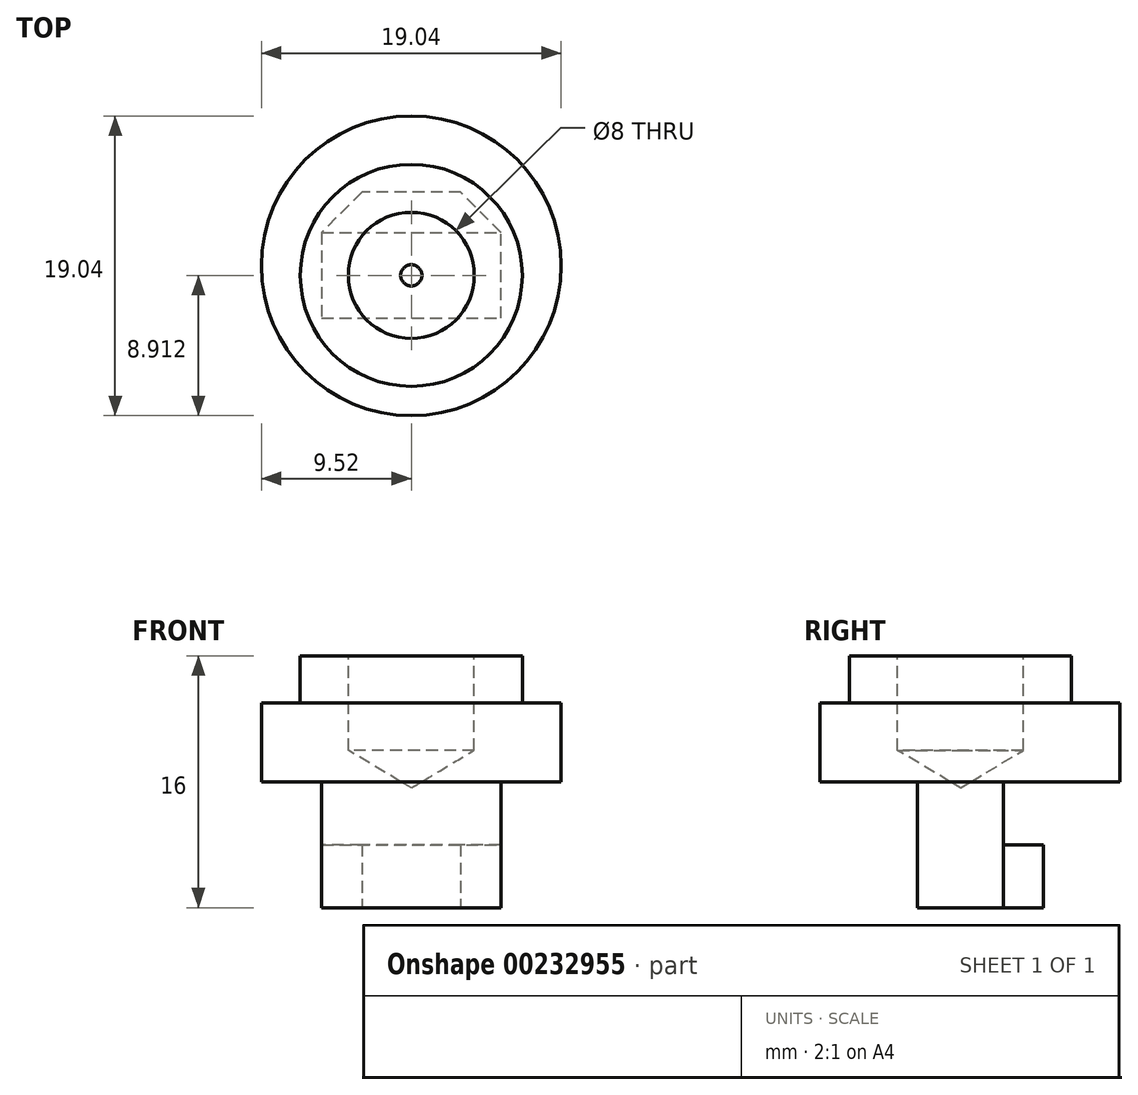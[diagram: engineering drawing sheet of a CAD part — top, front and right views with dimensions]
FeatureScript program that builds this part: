
annotation { "Feature Type Name" : "Feature", "Feature Type Description" : "" }
export const myFeature = defineFeature(function(context is Context, id is Id, definition is map)
    precondition{}
    {
        {
            var Q0;
            Q0=qCreatedBy(makeId("Top.planeOp"),FACE);
            var sketch = newSketch(context, id + "F4", { "sketchPlane" : qUnion([Q0])});
            skLineSegment(sketch, "E0", {"start": v(-5.7, -5.44) * mm, "end": v(5.7, -5.44) * mm});
            skLineSegment(sketch, "E1", {"start": v(5.7, -5.44) * mm, "end": v(5.7, 0) * mm});
            skLineSegment(sketch, "E2", {"start": v(5.7, 0) * mm, "end": v(3.14, 2.56) * mm});
            skLineSegment(sketch, "E3", {"start": v(3.14, 2.56) * mm, "end": v(-3.14, 2.56) * mm});
            skLineSegment(sketch, "E4", {"start": v(-3.14, 2.56) * mm, "end": v(-5.7, 0) * mm});
            skLineSegment(sketch, "E5", {"start": v(-5.7, 0) * mm, "end": v(-5.7, -5.44) * mm});
            skLineSegment(sketch, "E6", {"start": v(-3.14, 2.56) * mm, "end": v(-3.14, -5.44) * mm, "construction": true});
            skSolve(sketch);
        }
        {
            var Q0;
            Q0=makeQuery(id+"F4.imprint","IMPRINT",FACE,{"disambiguationData":[TD([[makeQuery(id+"F4.imprint","IMPRINT",EDGE,{"derivedFrom":sQuery(id+"F4.wireOp",EDGE,"E0")}),1.0]])]});
            extrude(context, id + "F0", {"entities" : qUnion([Q0]), "depth" : 4 * mm});
        }
        {
            var Q0;
            Q0=makeQuery(id+"F0.opExtrude","CAP_FACE",FACE,{"disambiguationData":[OSD([sQuery(id+"F4.wireOp",EDGE,"E0"),sQuery(id+"F4.wireOp",EDGE,"E1"),sQuery(id+"F4.wireOp",EDGE,"E2"),sQuery(id+"F4.wireOp",EDGE,"E3"),sQuery(id+"F4.wireOp",EDGE,"E4"),sQuery(id+"F4.wireOp",EDGE,"E5")])],"isStart":false});
            var sketch = newSketch(context, id + "F1", { "sketchPlane" : qUnion([Q0])});
            skLineSegment(sketch, "E7", {"start": v(-5.7, 0) * mm, "end": v(5.7, 0) * mm});
            skLineSegment(sketch, "E8", {"start": v(5.7, -5.44) * mm, "end": v(-5.7, -5.44) * mm});
            skLineSegment(sketch, "E9", {"start": v(-5.7, 0) * mm, "end": v(-5.7, 0) * mm});
            skLineSegment(sketch, "E10", {"start": v(-5.7, -5.44) * mm, "end": v(-5.7, 0) * mm});
            skLineSegment(sketch, "E11", {"start": v(5.7, 0) * mm, "end": v(5.7, -5.44) * mm});
            skSolve(sketch);
        }
        {
            var Q0;
            Q0=makeQuery(id+"F1.imprint","IMPRINT",FACE,{"disambiguationData":[TD([[makeQuery(id+"F1.imprint","IMPRINT",EDGE,{"derivedFrom":sQuery(id+"F1.wireOp",EDGE,"E7")}),-1.0]])]});
            extrude(context, id + "F2", {"entities" : qUnion([Q0]), "operationType" : NewBodyOperationType.ADD, "depth" : 4 * mm});
        }
        {
            var Q0;
            Q0=makeQuery(id+"F2.opExtrude","CAP_FACE",FACE,{"disambiguationData":[OSD([sQuery(id+"F1.wireOp",EDGE,"E7"),sQuery(id+"F1.wireOp",EDGE,"E8"),sQuery(id+"F1.wireOp",EDGE,"E10"),sQuery(id+"F1.wireOp",EDGE,"E11")])],"isStart":false});
            var sketch = newSketch(context, id + "F5", { "sketchPlane" : qUnion([Q0])});
            skCircle(sketch, "E12", {"center": v(0, -2.11) * mm, "radius": 9.52 * mm});
            skSolve(sketch);
        }
        {
            var Q0;
            Q0=makeQuery(id+"F5.imprint","IMPRINT",FACE,{"disambiguationData":[TD([[makeQuery(id+"F5.imprint","IMPRINT",EDGE,{"derivedFrom":makeQuery(id+"F2.opExtrude","CAP_EDGE",EDGE,{"disambiguationData":[OSD([sQuery(id+"F1.wireOp",EDGE,"E7")])],"isStart":false})}),-1.0]])]});
            var Q1;
            Q1=makeQuery(id+"F5.imprint","IMPRINT",FACE,{"disambiguationData":[TD([[makeQuery(id+"F5.imprint","IMPRINT",EDGE,{"derivedFrom":sQuery(id+"F5.wireOp",EDGE,"E12")}),1.0]])]});
            extrude(context, id + "F6", {"entities" : qUnion([Q0, Q1]), "depth" : 5 * mm});
        }
        {
            var Q0;
            Q0=makeQuery(id+"F6.opExtrude","CAP_FACE",FACE,{"disambiguationData":[OSD([sQuery(id+"F5.wireOp",EDGE,"E12")])],"isStart":false});
            var sketch = newSketch(context, id + "F7", { "sketchPlane" : qUnion([Q0])});
            skCircle(sketch, "E13", {"center": v(0, -2.72) * mm, "radius": 7.05 * mm});
            skSolve(sketch);
        }
        {
            var Q0;
            Q0 = qSketchRegion(id + "F7", true);
            extrude(context, id + "F3", {"entities" : qUnion([Q0]), "operationType" : NewBodyOperationType.ADD, "depth" : 3 * mm});
        }
        {
            var Q0;
            Q0=makeQuery(id+"F3.opExtrude","CAP_FACE",FACE,{"disambiguationData":[OSD([sQuery(id+"F7.wireOp",EDGE,"E13")])],"isStart":false});
            var sketch = newSketch(context, id + "F8", { "sketchPlane" : qUnion([Q0])});
            skCircle(sketch, "E14", {"center": v(0, -2.72) * mm, "radius": 3.87 * mm});
            skSolve(sketch);
        }
        {
            var Q0;
            Q0=sQuery(id+"F8.wireOp",VERTEX,"E14.center");
            var Q1;
            Q1=makeQuery(id+"F0.opExtrude","SWEPT_BODY",BODY,{"disambiguationData":[OSD([sQuery(id+"F4.wireOp",EDGE,"E0"),sQuery(id+"F4.wireOp",EDGE,"E1"),sQuery(id+"F4.wireOp",EDGE,"E2"),sQuery(id+"F4.wireOp",EDGE,"E3"),sQuery(id+"F4.wireOp",EDGE,"E4"),sQuery(id+"F4.wireOp",EDGE,"E5")])]});
            var Q2;
            Q2=makeQuery(id+"F6.opExtrude","SWEPT_BODY",BODY,{"disambiguationData":[OSD([sQuery(id+"F5.wireOp",EDGE,"E12")])]});
            hole(context, id + "F9", {"style" : HoleStyle.SIMPLE, "endStyle" : HoleEndStyle.BLIND, "holeDiameter" : 8 * mm, "holeDepth" : 6 * mm, "locations" : qUnion([Q0]), "scope" : qUnion([Q1, Q2])});
        }
    });
